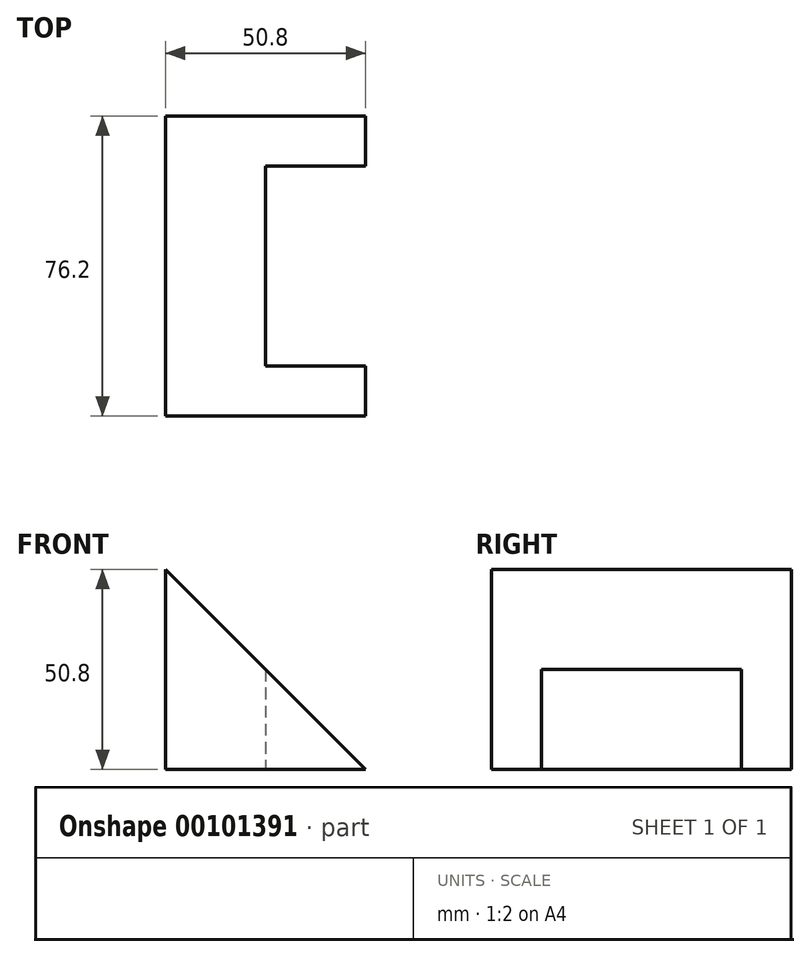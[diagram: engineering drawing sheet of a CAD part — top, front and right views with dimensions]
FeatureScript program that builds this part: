
annotation { "Feature Type Name" : "Feature", "Feature Type Description" : "" }
export const myFeature = defineFeature(function(context is Context, id is Id, definition is map)
    precondition{}
    {
        {
            var Q0;
            Q0=qCreatedBy(makeId("Front.planeOp"),FACE);
            var sketch = newSketch(context, id + "F0", { "sketchPlane" : qUnion([Q0])});
            skLineSegment(sketch, "E0", {"start": v(0, 0) * mm, "end": v(0, 50.8) * mm});
            skLineSegment(sketch, "E1", {"start": v(0, 50.8) * mm, "end": v(50.8, 0) * mm});
            skLineSegment(sketch, "E2", {"start": v(50.8, 0) * mm, "end": v(0, 0) * mm});
            skSolve(sketch);
        }
        {
            var Q0;
            Q0=makeQuery(id+"F0.imprint","IMPRINT",FACE,{"disambiguationData":[TD([[makeQuery(id+"F0.imprint","IMPRINT",EDGE,{"derivedFrom":sQuery(id+"F0.wireOp",EDGE,"E0")}),-1.0]])]});
            var sketch = newSketch(context, id + "F1", { "sketchPlane" : qUnion([Q0])});
            skLineSegment(sketch, "E3", {"start": v(50.8, 0) * mm, "end": v(25.4, 25.4) * mm});
            skLineSegment(sketch, "E4", {"start": v(25.4, 25.4) * mm, "end": v(25.4, 0) * mm});
            skLineSegment(sketch, "E5", {"start": v(25.4, 0) * mm, "end": v(50.8, 0) * mm});
            skSolve(sketch);
        }
        {
            var Q0;
            Q0 = qSketchRegion(id + "F0", true);
            extrude(context, id + "F2", {"entities" : qUnion([Q0]), "endBound" : BoundingType.SYMMETRIC, "depth" : 76.2 * mm});
        }
        {
            var Q0;
            Q0 = qSketchRegion(id + "F1", true);
            extrude(context, id + "F3", {"entities" : qUnion([Q0]), "operationType" : NewBodyOperationType.REMOVE, "endBound" : BoundingType.SYMMETRIC, "depth" : 50.8 * mm});
        }
    });
